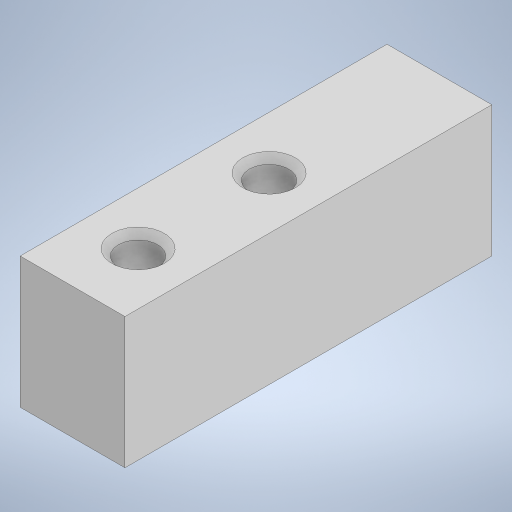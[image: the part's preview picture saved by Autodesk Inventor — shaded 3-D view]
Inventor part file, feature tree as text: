
AUTODESK INVENTOR PART (.ipt)
format: ipt  version: 2023 (Build 270158000, 158)  size: 204,800 bytes
history: native  units: mm
features: other x1, extrude x1, chamfer x1, sketch x1
ambient origin geometry x8: Origin, YZ Plane, XZ Plane, XY Plane, X Axis, Y Axis, Z Axis, Center Point
bodies: Body1 (feature_tree)
feature tree (4):
  other  "Твердое тело1"
  extrude  "Выдавливание1"  Depth=8.0mm
  chamfer  "Фаска1"  Distance=28.0mm
  sketch  "Эскиз1"
